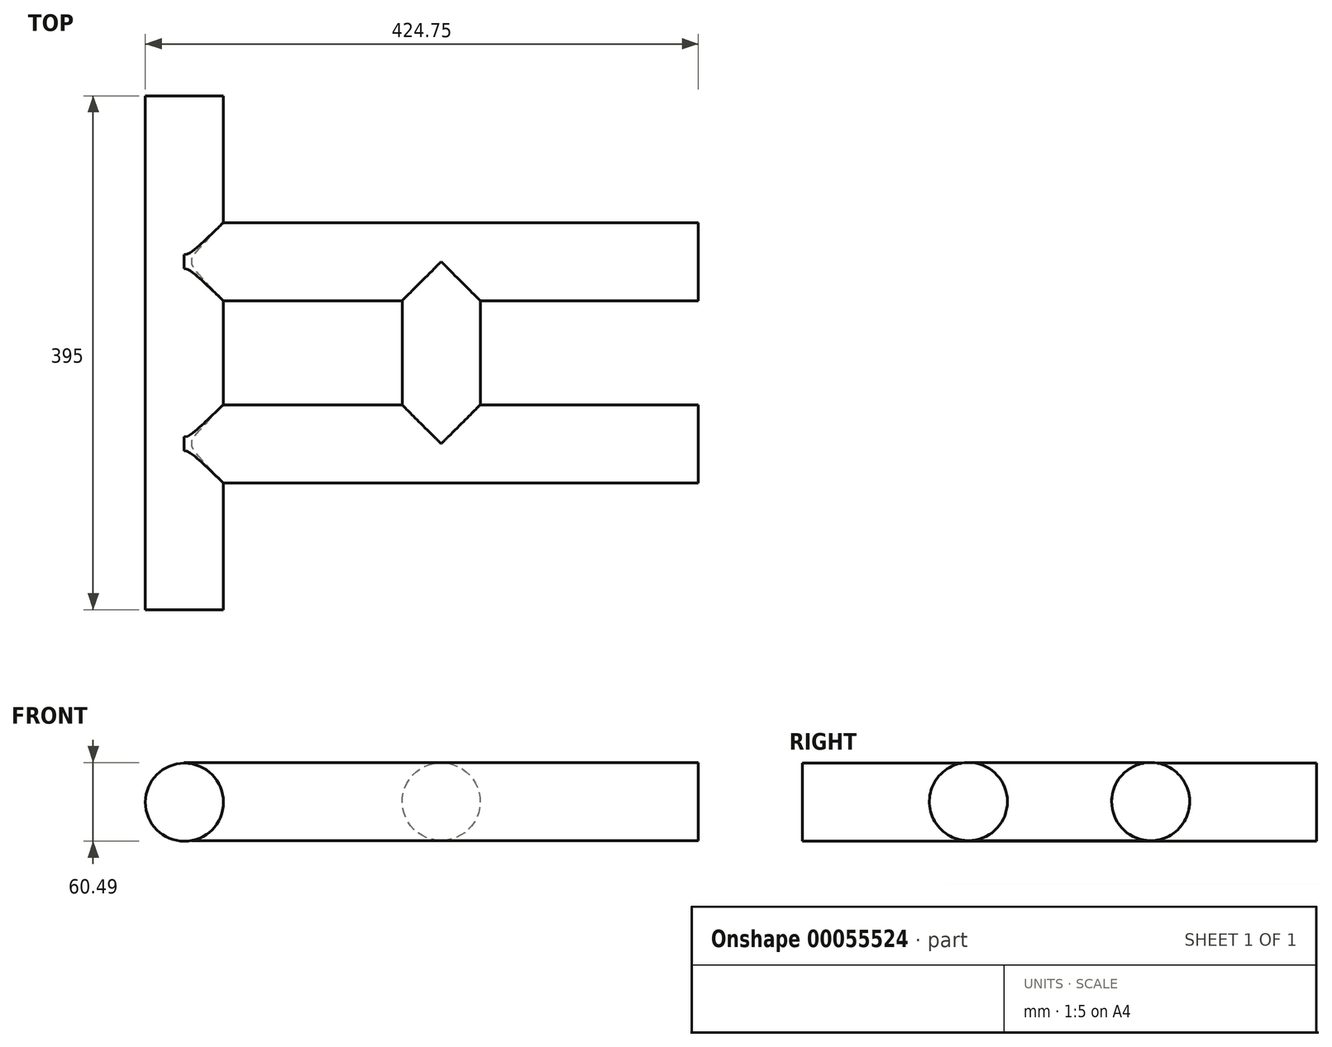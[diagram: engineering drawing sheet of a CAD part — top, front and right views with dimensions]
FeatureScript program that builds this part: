
annotation { "Feature Type Name" : "Feature", "Feature Type Description" : "" }
export const myFeature = defineFeature(function(context is Context, id is Id, definition is map)
    precondition{}
    {
        {
            var Q0;
            Q0=qCreatedBy(makeId("Front.planeOp"),FACE);
            var sketch = newSketch(context, id + "F0", { "sketchPlane" : qUnion([Q0])});
            skCircle(sketch, "E0", {"center": v(0, 0) * mm, "radius": 30 * mm});
            skCircle(sketch, "E1", {"center": v(-197.25, -0.49) * mm, "radius": 30 * mm});
            skCircle(sketch, "E2.MirrorC", {"center": v(197.25, -0.49) * mm, "radius": 30 * mm});
            skSolve(sketch);
        }
        {
            var Q0;
            Q0=makeQuery(id+"F0.imprint","IMPRINT",FACE,{"disambiguationData":[TD([[makeQuery(id+"F0.imprint","IMPRINT",EDGE,{"derivedFrom":sQuery(id+"F0.wireOp",EDGE,"E1")}),1.0]])]});
            var Q1;
            Q1=makeQuery(id+"F0.imprint","IMPRINT",FACE,{"disambiguationData":[TD([[makeQuery(id+"F0.imprint","IMPRINT",EDGE,{"derivedFrom":sQuery(id+"F0.wireOp",EDGE,"E2.MirrorC")}),-1.0]])]});
            extrude(context, id + "F1", {"entities" : qUnion([Q0, Q1]), "endBound" : BoundingType.SYMMETRIC, "depth" : 395 * mm});
        }
        {
            var Q0;
            Q0=makeQuery(id+"F0.imprint","IMPRINT",FACE,{"disambiguationData":[TD([[makeQuery(id+"F0.imprint","IMPRINT",EDGE,{"derivedFrom":sQuery(id+"F0.wireOp",EDGE,"E0")}),1.0]])]});
            extrude(context, id + "F2", {"entities" : qUnion([Q0]), "endBound" : BoundingType.SYMMETRIC, "depth" : 140 * mm});
        }
        {
            var Q0;
            Q0=qCreatedBy(makeId("Right.planeOp"),FACE);
            var sketch = newSketch(context, id + "F3", { "sketchPlane" : qUnion([Q0])});
            skLineSegment(sketch, "E3.0", {"start": v(-70, -30) * mm, "end": v(-70, 30) * mm});
            skLineSegment(sketch, "E4.0", {"start": v(70, -30) * mm, "end": v(70, 30) * mm});
            skCircle(sketch, "E5", {"center": v(-70, 0) * mm, "radius": 30 * mm});
            skCircle(sketch, "E6", {"center": v(70, 0) * mm, "radius": 30 * mm});
            skSolve(sketch);
        }
        {
            var Q0;
            {var subQ0=sQuery(id+"F3.wireOp",EDGE,"E3.0");Q0=makeQuery(id+"F3.imprint","IMPRINT",FACE,{"disambiguationData":[TD([[makeQuery(id+"F3.imprint","IMPRINT",EDGE,{"derivedFrom":subQ0}),-1.0]])]});}
            var Q1;
            {var subQ0=sQuery(id+"F3.wireOp",EDGE,"E4.0");Q1=makeQuery(id+"F3.imprint","IMPRINT",FACE,{"disambiguationData":[TD([[makeQuery(id+"F3.imprint","IMPRINT",EDGE,{"derivedFrom":subQ0}),1.0]])]});}
            var Q2;
            {var subQ0=sQuery(id+"F3.wireOp",EDGE,"E3.0");Q2=makeQuery(id+"F3.imprint","IMPRINT",FACE,{"disambiguationData":[TD([[makeQuery(id+"F3.imprint","IMPRINT",EDGE,{"derivedFrom":subQ0}),1.0]])]});}
            var Q3;
            {var subQ0=sQuery(id+"F3.wireOp",EDGE,"E4.0");Q3=makeQuery(id+"F3.imprint","IMPRINT",FACE,{"disambiguationData":[TD([[makeQuery(id+"F3.imprint","IMPRINT",EDGE,{"derivedFrom":subQ0}),-1.0]])]});}
            extrude(context, id + "F4", {"entities" : qUnion([Q0, Q1, Q2, Q3]), "operationType" : NewBodyOperationType.ADD, "endBound" : BoundingType.SYMMETRIC, "depth" : 395 * mm});
        }
    });
